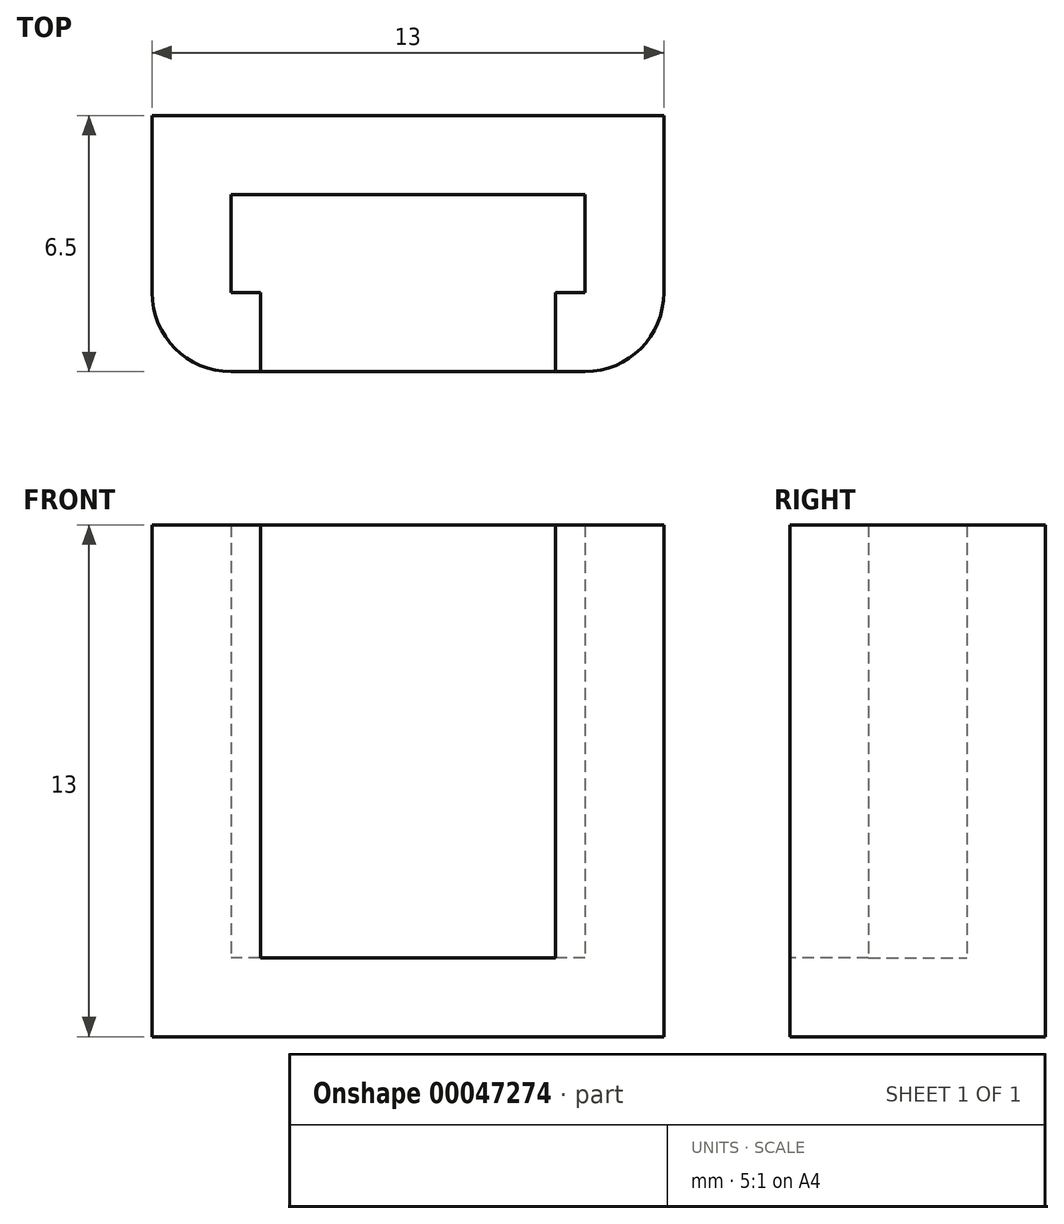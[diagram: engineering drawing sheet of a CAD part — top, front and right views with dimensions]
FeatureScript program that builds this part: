
annotation { "Feature Type Name" : "Feature", "Feature Type Description" : "" }
export const myFeature = defineFeature(function(context is Context, id is Id, definition is map)
    precondition{}
    {
        {
            var Q0;
            Q0=qCreatedBy(makeId("Top.planeOp"),FACE);
            var sketch = newSketch(context, id + "F0", { "sketchPlane" : qUnion([Q0])});
            skLineSegment(sketch, "E0.bottom", {"start": v(6.5, -3.25) * mm, "end": v(-6.5, -3.25) * mm});
            skLineSegment(sketch, "E0.top", {"start": v(6.5, 3.25) * mm, "end": v(-6.5, 3.25) * mm});
            skLineSegment(sketch, "E0.left", {"start": v(6.5, -3.25) * mm, "end": v(6.5, 3.25) * mm});
            skLineSegment(sketch, "E0.right", {"start": v(-6.5, -3.25) * mm, "end": v(-6.5, 3.25) * mm});
            skPoint(sketch, "E0.middle", {"position": v(0, 0) * mm});
            skLineSegment(sketch, "E1.bottom", {"start": v(4.5, -1.25) * mm, "end": v(-4.5, -1.25) * mm});
            skLineSegment(sketch, "E1.top", {"start": v(4.5, 1.25) * mm, "end": v(-4.5, 1.25) * mm});
            skLineSegment(sketch, "E1.left", {"start": v(4.5, -1.25) * mm, "end": v(4.5, 1.25) * mm});
            skLineSegment(sketch, "E1.right", {"start": v(-4.5, -1.25) * mm, "end": v(-4.5, 1.25) * mm});
            skLineSegment(sketch, "E2", {"start": v(-3.75, -1.25) * mm, "end": v(-3.75, -3.25) * mm});
            skLineSegment(sketch, "E3", {"start": v(3.75, -1.25) * mm, "end": v(3.75, -3.25) * mm});
            skSolve(sketch);
        }
        {
            var Q0;
            Q0=makeQuery(id+"F0.imprint","IMPRINT",FACE,{"disambiguationData":[TD([[makeQuery(id+"F0.imprint","IMPRINT",EDGE,{"derivedFrom":sQuery(id+"F0.wireOp",EDGE,"E0.top")}),1.0]])]});
            extrude(context, id + "F1", {"entities" : qUnion([Q0]), "depth" : 13 * mm});
        }
        {
            var Q0;
            Q0=makeQuery(id+"F0.imprint","IMPRINT",FACE,{"disambiguationData":[TD([[makeQuery(id+"F0.imprint","IMPRINT",EDGE,{"derivedFrom":sQuery(id+"F0.wireOp",EDGE,"E0.top")}),1.0]])]});
            var Q1;
            Q1=makeQuery(id+"F0.imprint","IMPRINT",FACE,{"disambiguationData":[TD([[makeQuery(id+"F0.imprint","IMPRINT",EDGE,{"derivedFrom":sQuery(id+"F0.wireOp",EDGE,"E1.top")}),1.0]])]});
            var Q2;
            {var subQ0=sQuery(id+"F0.wireOp",EDGE,"E2");Q2=makeQuery(id+"F0.imprint","IMPRINT",FACE,{"disambiguationData":[TD([[makeQuery(id+"F0.imprint","IMPRINT",EDGE,{"derivedFrom":subQ0}),1.0]])]});}
            extrude(context, id + "F2", {"entities" : qUnion([Q0, Q1, Q2]), "operationType" : NewBodyOperationType.ADD, "depth" : 2 * mm});
        }
        {
            var Q0;
            Q0=makeQuery(id+"F1.opExtrude","SWEPT_EDGE",EDGE,{"disambiguationData":[OSD([sQuery(id+"F0.wireOp",EDGE,"E0.bottom"),sQuery(id+"F0.wireOp",EDGE,"E0.right")])]});
            var Q1;
            Q1=makeQuery(id+"F1.opExtrude","SWEPT_EDGE",EDGE,{"disambiguationData":[OSD([sQuery(id+"F0.wireOp",EDGE,"E0.bottom"),sQuery(id+"F0.wireOp",EDGE,"E0.left")])]});
            fillet(context, id + "F3", {"entities" : qUnion([Q0, Q1]), "radius" : 2 * mm, "tangentPropagation" : true, "allowEdgeOverflow" : false});
        }
    });
